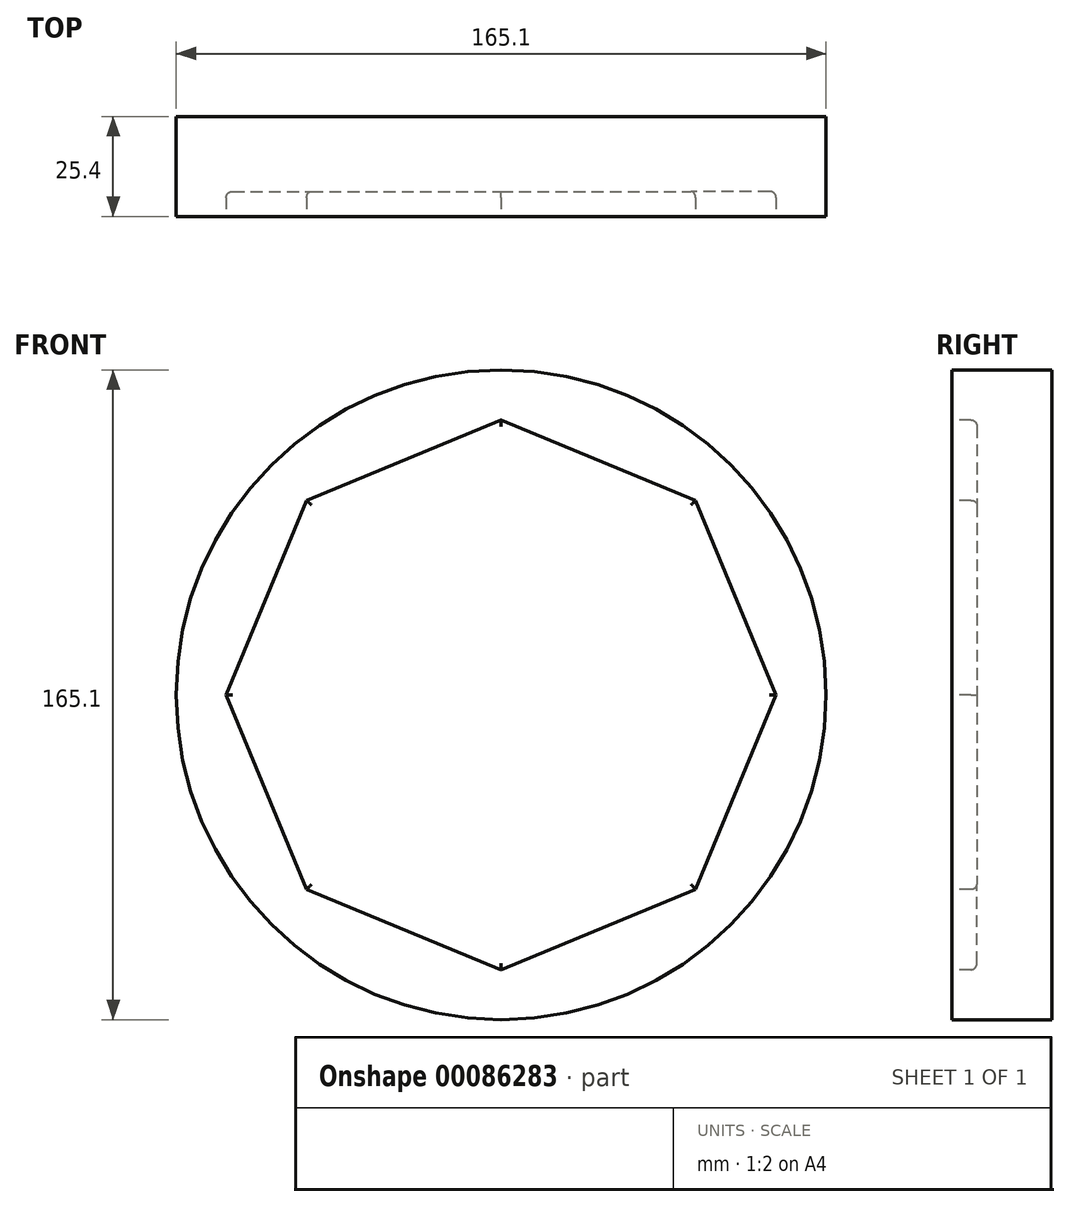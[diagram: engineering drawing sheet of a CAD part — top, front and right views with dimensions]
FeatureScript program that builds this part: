
annotation { "Feature Type Name" : "Feature", "Feature Type Description" : "" }
export const myFeature = defineFeature(function(context is Context, id is Id, definition is map)
    precondition{}
    {
        {
            var Q0;
            Q0=qCreatedBy(makeId("Front.planeOp"),FACE);
            var sketch = newSketch(context, id + "F0", { "sketchPlane" : qUnion([Q0])});
            skCircle(sketch, "E0", {"center": v(0, 0) * mm, "radius": 82.55 * mm});
            skSolve(sketch);
        }
        {
            var Q0;
            Q0=qSketchRegion(id+"F0",true);
            extrude(context, id + "F1", {"entities" : qUnion([Q0]), "depth" : 25.4 * mm});
        }
        {
            var Q0;
            Q0=makeQuery(id+"F1.opExtrude","CAP_FACE",FACE,{"disambiguationData":[OSD([sQuery(id+"F0.wireOp",EDGE,"E0")])],"isStart":false});
            var sketch = newSketch(context, id + "F2", { "sketchPlane" : qUnion([Q0])});
            skCircle(sketch, "E1.cCircle", {"center": v(0, 0) * mm, "radius": 69.85 * mm, "construction": true});
            skLineSegment(sketch, "E1.0", {"start": v(69.85, 0) * mm, "end": v(49.4, -49.4) * mm});
            skLineSegment(sketch, "E1.1", {"start": v(49.4, -49.4) * mm, "end": v(0, -69.85) * mm});
            skLineSegment(sketch, "E1.2", {"start": v(0, -69.85) * mm, "end": v(-49.4, -49.4) * mm});
            skLineSegment(sketch, "E1.3", {"start": v(-49.4, -49.4) * mm, "end": v(-69.85, 0) * mm});
            skLineSegment(sketch, "E1.4", {"start": v(-69.85, 0) * mm, "end": v(-49.4, 49.4) * mm});
            skLineSegment(sketch, "E1.5", {"start": v(-49.4, 49.4) * mm, "end": v(0, 69.85) * mm});
            skLineSegment(sketch, "E1.6", {"start": v(0, 69.85) * mm, "end": v(49.4, 49.4) * mm});
            skLineSegment(sketch, "E1.7", {"start": v(49.4, 49.4) * mm, "end": v(69.85, 0) * mm});
            skSolve(sketch);
        }
        {
            var Q0;
            Q0=qSketchRegion(id+"F2",true);
            extrude(context, id + "F3", {"entities" : qUnion([Q0]), "operationType" : NewBodyOperationType.REMOVE, "oppositeDirection" : true, "depth" : 6.35 * mm});
        }
        {
            var Q0;
            Q0=makeQuery(id+"F3.boolean.opBoolean","COPY",FACE,{"derivedFrom":makeQuery(id+"F3.opExtrude","CAP_FACE",FACE,{"disambiguationData":[OSD([sQuery(id+"F2.wireOp",EDGE,"E1.0"),sQuery(id+"F2.wireOp",EDGE,"E1.1"),sQuery(id+"F2.wireOp",EDGE,"E1.2"),sQuery(id+"F2.wireOp",EDGE,"E1.3"),sQuery(id+"F2.wireOp",EDGE,"E1.4"),sQuery(id+"F2.wireOp",EDGE,"E1.5"),sQuery(id+"F2.wireOp",EDGE,"E1.6"),sQuery(id+"F2.wireOp",EDGE,"E1.7")])],"isStart":false})});
            var Q1;
            Q1=makeQuery(id+"F3.boolean.opBoolean","COPY",EDGE,{"derivedFrom":makeQuery(id+"F3.opExtrude","CAP_EDGE",EDGE,{"disambiguationData":[OSD([sQuery(id+"F2.wireOp",EDGE,"E1.4")])],"isStart":true})});
            var Q2;
            Q2=makeQuery(id+"F3.boolean.opBoolean","COPY",EDGE,{"derivedFrom":makeQuery(id+"F3.opExtrude","CAP_EDGE",EDGE,{"disambiguationData":[OSD([sQuery(id+"F2.wireOp",EDGE,"E1.5")])],"isStart":true})});
            var Q3;
            Q3=makeQuery(id+"F3.boolean.opBoolean","COPY",EDGE,{"derivedFrom":makeQuery(id+"F3.opExtrude","CAP_EDGE",EDGE,{"disambiguationData":[OSD([sQuery(id+"F2.wireOp",EDGE,"E1.6")])],"isStart":true})});
            var Q4;
            Q4=makeQuery(id+"F3.boolean.opBoolean","COPY",EDGE,{"derivedFrom":makeQuery(id+"F3.opExtrude","CAP_EDGE",EDGE,{"disambiguationData":[OSD([sQuery(id+"F2.wireOp",EDGE,"E1.7")])],"isStart":true})});
            var Q5;
            Q5=makeQuery(id+"F3.boolean.opBoolean","COPY",EDGE,{"derivedFrom":makeQuery(id+"F3.opExtrude","CAP_EDGE",EDGE,{"disambiguationData":[OSD([sQuery(id+"F2.wireOp",EDGE,"E1.0")])],"isStart":true})});
            var Q6;
            Q6=makeQuery(id+"F3.boolean.opBoolean","COPY",EDGE,{"derivedFrom":makeQuery(id+"F3.opExtrude","CAP_EDGE",EDGE,{"disambiguationData":[OSD([sQuery(id+"F2.wireOp",EDGE,"E1.1")])],"isStart":true})});
            var Q7;
            Q7=makeQuery(id+"F3.boolean.opBoolean","COPY",EDGE,{"derivedFrom":makeQuery(id+"F3.opExtrude","CAP_EDGE",EDGE,{"disambiguationData":[OSD([sQuery(id+"F2.wireOp",EDGE,"E1.2")])],"isStart":true})});
            var Q8;
            Q8=makeQuery(id+"F3.boolean.opBoolean","COPY",EDGE,{"derivedFrom":makeQuery(id+"F3.opExtrude","CAP_EDGE",EDGE,{"disambiguationData":[OSD([sQuery(id+"F2.wireOp",EDGE,"E1.3")])],"isStart":true})});
            fillet(context, id + "F4", {"entities" : qUnion([Q0, Q1, Q2, Q3, Q4, Q5, Q6, Q7, Q8]), "radius" : 1.52 * mm, "tangentPropagation" : true, "allowEdgeOverflow" : false});
        }
    });
